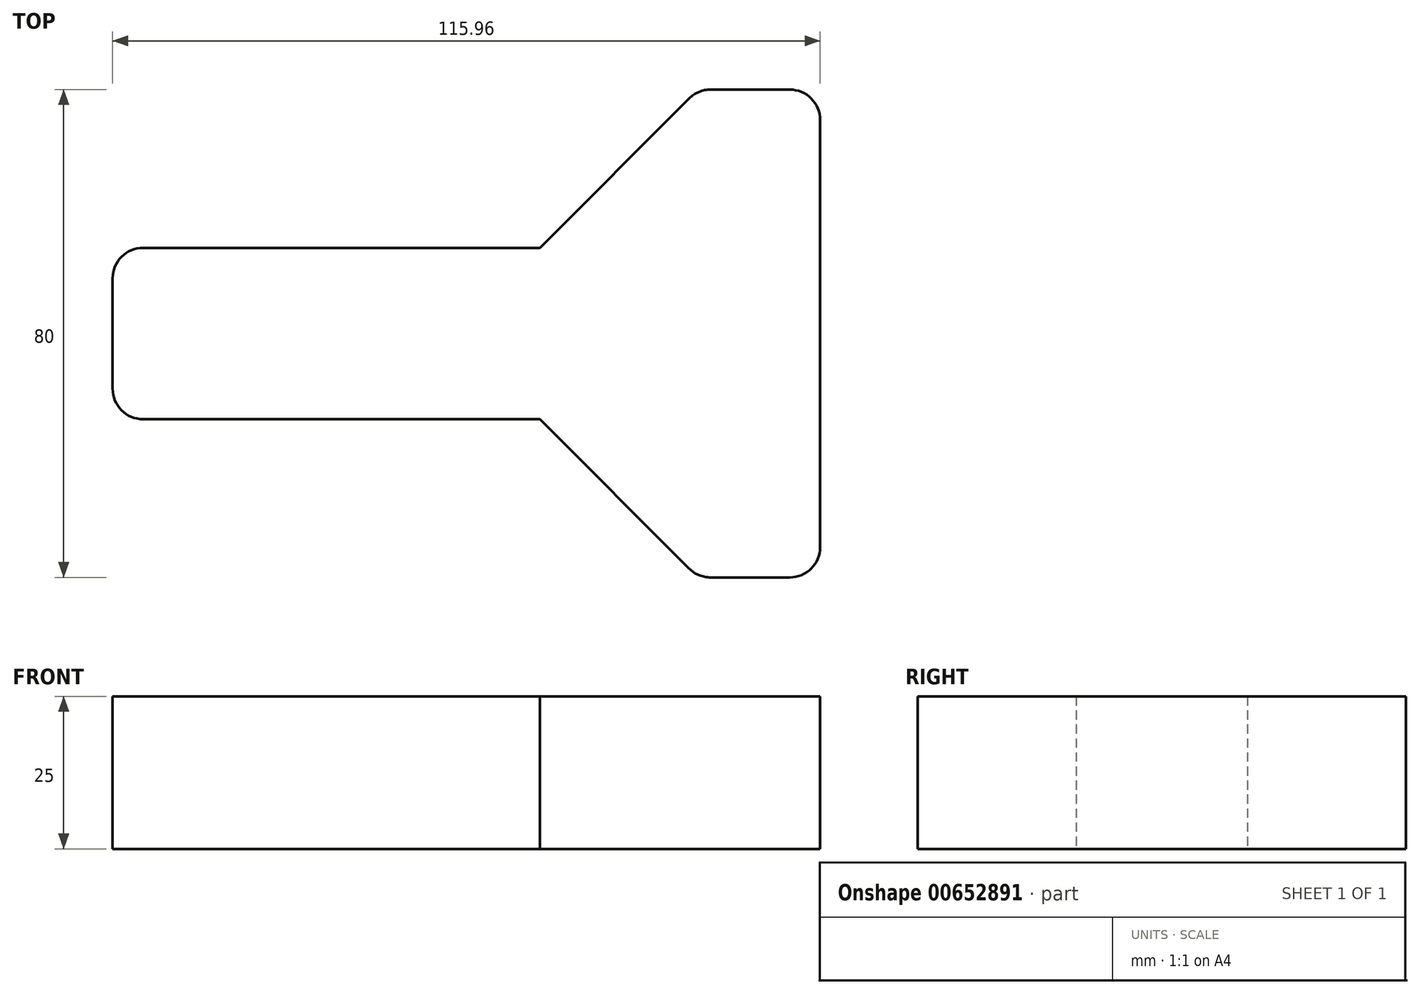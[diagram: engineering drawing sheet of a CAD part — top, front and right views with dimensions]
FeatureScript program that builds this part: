
annotation { "Feature Type Name" : "Feature", "Feature Type Description" : "" }
export const myFeature = defineFeature(function(context is Context, id is Id, definition is map)
    precondition{}
    {
        {
            var Q0;
            Q0=qCreatedBy(makeId("Top.planeOp"),FACE);
            var sketch = newSketch(context, id + "F0", { "sketchPlane" : qUnion([Q0])});
            skLineSegment(sketch, "E0", {"start": v(-70, 0) * mm, "end": v(-70, 14.04) * mm});
            skLineSegment(sketch, "E1", {"start": v(-70, 14.04) * mm, "end": v(0, 14.04) * mm});
            skLineSegment(sketch, "E2", {"start": v(0, 14.04) * mm, "end": v(25.96, 40) * mm});
            skLineSegment(sketch, "E3", {"start": v(25.96, 40) * mm, "end": v(45.96, 40) * mm});
            skLineSegment(sketch, "E4", {"start": v(45.96, 40) * mm, "end": v(45.96, 0) * mm});
            skLineSegment(sketch, "E5.MirrorCS", {"start": v(-70, 0) * mm, "end": v(-70, -14.04) * mm});
            skLineSegment(sketch, "E6.MirrorCS", {"start": v(-70, -14.04) * mm, "end": v(0, -14.04) * mm});
            skLineSegment(sketch, "E7.MirrorCS", {"start": v(0, -14.04) * mm, "end": v(25.96, -40) * mm});
            skLineSegment(sketch, "E8.MirrorCS", {"start": v(25.96, -40) * mm, "end": v(45.96, -40) * mm});
            skLineSegment(sketch, "E9.MirrorCS", {"start": v(45.96, -40) * mm, "end": v(45.96, 0) * mm});
            skSolve(sketch);
        }
        {
            var Q0;
            Q0=makeQuery(id+"F0.imprint","IMPRINT",FACE,{"disambiguationData":[TD([[makeQuery(id+"F0.imprint","IMPRINT",EDGE,{"derivedFrom":sQuery(id+"F0.wireOp",EDGE,"E0")}),-1.0]])]});
            extrude(context, id + "F1", {"entities" : qUnion([Q0]), "depth" : 25 * mm, "offsetDistance" : 25 * mm});
        }
        {
            var Q0;
            Q0=makeQuery(id+"F1.opExtrude","SWEPT_EDGE",EDGE,{"disambiguationData":[OSD([sQuery(id+"F0.wireOp",EDGE,"E5.MirrorCS"),sQuery(id+"F0.wireOp",EDGE,"E6.MirrorCS")])]});
            var Q1;
            Q1=makeQuery(id+"F1.opExtrude","SWEPT_EDGE",EDGE,{"disambiguationData":[OSD([sQuery(id+"F0.wireOp",EDGE,"E0"),sQuery(id+"F0.wireOp",EDGE,"E1")])]});
            var Q2;
            Q2=makeQuery(id+"F1.opExtrude","SWEPT_EDGE",EDGE,{"disambiguationData":[OSD([sQuery(id+"F0.wireOp",EDGE,"E7.MirrorCS"),sQuery(id+"F0.wireOp",EDGE,"E8.MirrorCS")])]});
            var Q3;
            Q3=makeQuery(id+"F1.opExtrude","SWEPT_EDGE",EDGE,{"disambiguationData":[OSD([sQuery(id+"F0.wireOp",EDGE,"E2"),sQuery(id+"F0.wireOp",EDGE,"E3")])]});
            var Q4;
            Q4=makeQuery(id+"F1.opExtrude","SWEPT_EDGE",EDGE,{"disambiguationData":[OSD([sQuery(id+"F0.wireOp",EDGE,"E3"),sQuery(id+"F0.wireOp",EDGE,"E4")])]});
            var Q5;
            Q5=makeQuery(id+"F1.opExtrude","SWEPT_EDGE",EDGE,{"disambiguationData":[OSD([sQuery(id+"F0.wireOp",EDGE,"E8.MirrorCS"),sQuery(id+"F0.wireOp",EDGE,"E9.MirrorCS")])]});
            fillet(context, id + "F2", {"entities" : qUnion([Q0, Q1, Q2, Q3, Q4, Q5]), "radius" : 5 * mm, "tangentPropagation" : true, "allowEdgeOverflow" : false});
        }
    });
